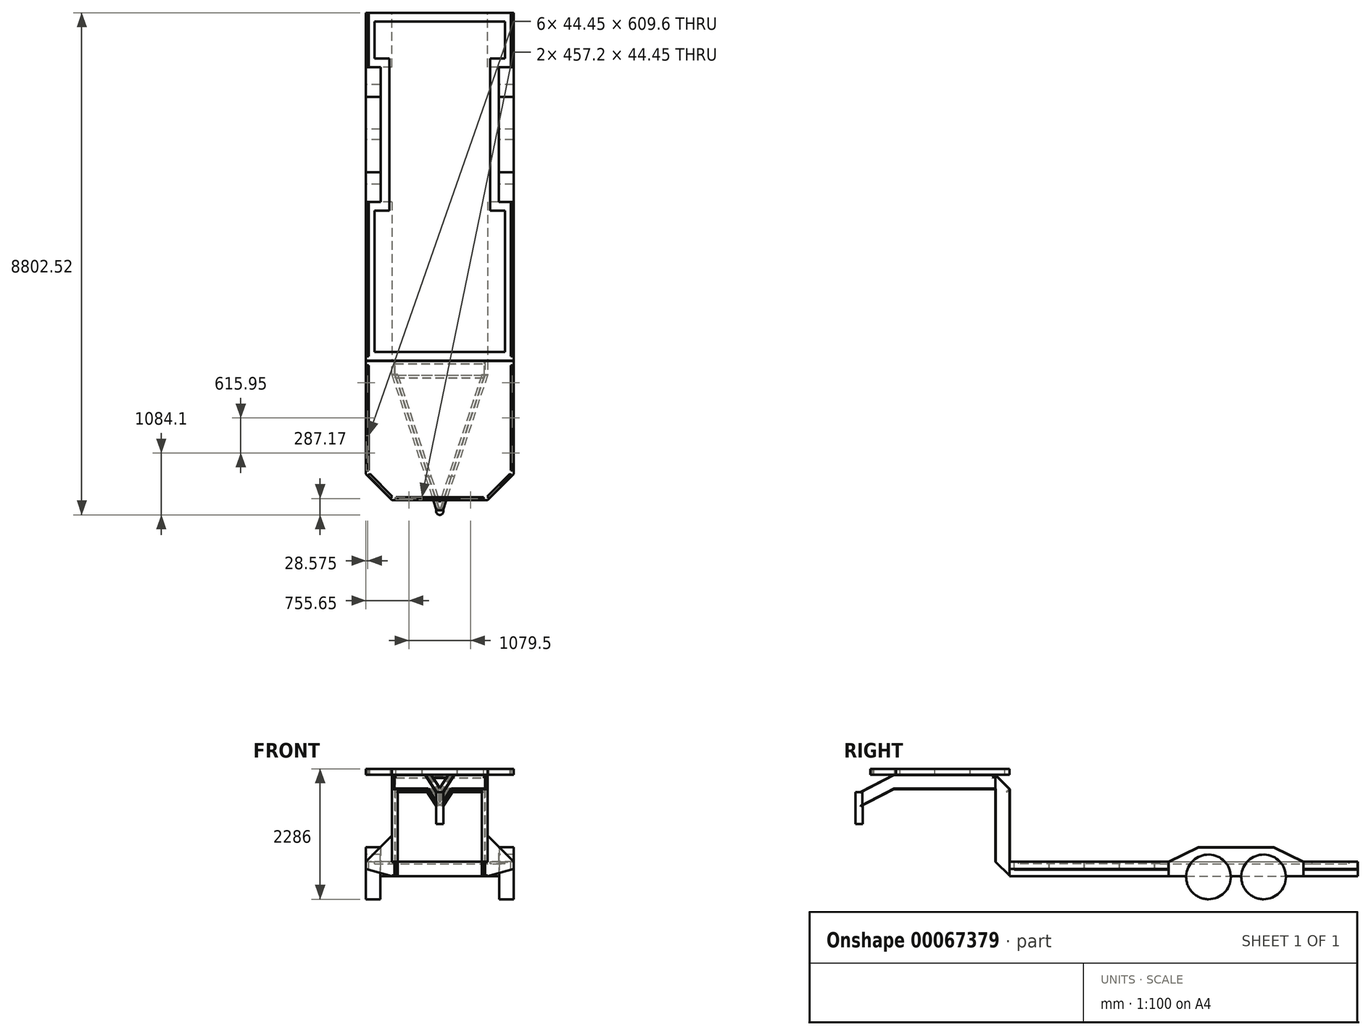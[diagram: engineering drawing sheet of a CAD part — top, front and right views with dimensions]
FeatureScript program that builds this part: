
annotation { "Feature Type Name" : "Feature", "Feature Type Description" : "" }
export const myFeature = defineFeature(function(context is Context, id is Id, definition is map)
    precondition{}
    {
        {
            var Q0;
            Q0=qCreatedBy(makeId("Front.planeOp"),FACE);
            var sketch = newSketch(context, id + "F0", { "sketchPlane" : qUnion([Q0])});
            skLineSegment(sketch, "E0.rect.bottom", {"start": v(1295.4, 660.4) * mm, "end": v(-1295.4, 660.4) * mm});
            skLineSegment(sketch, "E0.rect.top", {"start": v(1295.4, 406.4) * mm, "end": v(-1295.4, 406.4) * mm});
            skLineSegment(sketch, "E0.rect.left", {"start": v(1295.4, 660.4) * mm, "end": v(1295.4, 406.4) * mm});
            skLineSegment(sketch, "E0.rect.right", {"start": v(-1295.4, 660.4) * mm, "end": v(-1295.4, 406.4) * mm});
            skPoint(sketch, "E0.rect.middle", {"position": v(0, 533.4) * mm});
            skSolve(sketch);
        }
        {
            var Q0;
            Q0 = qSketchRegion(id + "F0", true);
            extrude(context, id + "F1", {"entities" : qUnion([Q0]), "depth" : 6096 * mm});
        }
        {
            var Q0;
            Q0=makeQuery(id+"F1.opExtrude","SWEPT_FACE",FACE,{"disambiguationData":[OSD([sQuery(id+"F0.wireOp",EDGE,"E0.rect.left")])]});
            var sketch = newSketch(context, id + "F2", { "sketchPlane" : qUnion([Q0])});
            skLineSegment(sketch, "E1", {"start": v(-3314.7, 660.4) * mm, "end": v(-2793.92, 914.4) * mm});
            skLineSegment(sketch, "E2", {"start": v(-2793.92, 914.4) * mm, "end": v(-1473.28, 914.4) * mm});
            skLineSegment(sketch, "E3", {"start": v(-1473.28, 914.4) * mm, "end": v(-952.5, 660.4) * mm});
            skLineSegment(sketch, "E4", {"start": v(-952.5, 660.4) * mm, "end": v(-3314.7, 660.4) * mm});
            skLineSegment(sketch, "E5", {"start": v(-2133.6, 660.4) * mm, "end": v(-2133.6, 406.4) * mm, "construction": true});
            skSolve(sketch);
        }
        {
            var Q0;
            Q0=makeQuery(id+"F2.imprint","IMPRINT",FACE,{"disambiguationData":[TD([[makeQuery(id+"F2.imprint","IMPRINT",EDGE,{"derivedFrom":sQuery(id+"F2.wireOp",EDGE,"E1")}),-1.0]])]});
            var Q1;
            Q1=makeQuery(id+"F1.opExtrude","SWEPT_FACE",FACE,{"disambiguationData":[OSD([sQuery(id+"F0.wireOp",EDGE,"E0.rect.right")])]});
            extrude(context, id + "F3", {"entities" : qUnion([Q0]), "operationType" : NewBodyOperationType.ADD, "endBound" : BoundingType.UP_TO_SURFACE, "oppositeDirection" : true, "endBoundEntityFace" : qUnion([Q1]), "depth" : 25.4 * mm});
        }
        {
            var Q0;
            Q0=makeQuery(id+"F3.boolean.opBoolean","MERGE",FACE,{"derivedFrom":[makeQuery(id+"F1.opExtrude","SWEPT_FACE",FACE,{"disambiguationData":[OSD([sQuery(id+"F0.wireOp",EDGE,"E0.rect.right")])]}),makeQuery(id+"F3.opExtrude","CAP_FACE",FACE,{"disambiguationData":[OSD([sQuery(id+"F2.wireOp",EDGE,"E1"),sQuery(id+"F2.wireOp",EDGE,"E2"),sQuery(id+"F2.wireOp",EDGE,"E3"),sQuery(id+"F2.wireOp",EDGE,"E4")])],"isStart":false})]});
            var sketch = newSketch(context, id + "F4", { "sketchPlane" : qUnion([Q0])});
            skCircle(sketch, "E6", {"center": v(1651, 391.16) * mm, "radius": 391.16 * mm});
            skCircle(sketch, "E7", {"center": v(2616.2, 391.16) * mm, "radius": 391.16 * mm});
            skLineSegment(sketch, "E8", {"start": v(2133.6, 914.4) * mm, "end": v(2133.6, 391.16) * mm, "construction": true});
            skLineSegment(sketch, "E9", {"start": v(1651, 391.16) * mm, "end": v(2616.2, 391.16) * mm, "construction": true});
            skSolve(sketch);
        }
        {
            var Q0;
            Q0 = qSketchRegion(id + "F4", true);
            var Q1;
            Q1=makeQuery(id+"F3.boolean.opBoolean","MERGE",FACE,{"derivedFrom":[makeQuery(id+"F1.opExtrude","SWEPT_FACE",FACE,{"disambiguationData":[OSD([sQuery(id+"F0.wireOp",EDGE,"E0.rect.left")])]}),makeQuery(id+"F3.opExtrude","CAP_FACE",FACE,{"disambiguationData":[OSD([sQuery(id+"F2.wireOp",EDGE,"E1"),sQuery(id+"F2.wireOp",EDGE,"E2"),sQuery(id+"F2.wireOp",EDGE,"E3"),sQuery(id+"F2.wireOp",EDGE,"E4")])],"isStart":true})]});
            extrude(context, id + "F5", {"entities" : qUnion([Q0]), "operationType" : NewBodyOperationType.ADD, "endBound" : BoundingType.UP_TO_SURFACE, "oppositeDirection" : true, "endBoundEntityFace" : qUnion([Q1]), "depth" : 25.4 * mm});
        }
        {
            var Q0;
            Q0=makeQuery(id+"F1.opExtrude","CAP_FACE",FACE,{"disambiguationData":[OSD([sQuery(id+"F0.wireOp",EDGE,"E0.rect.bottom"),sQuery(id+"F0.wireOp",EDGE,"E0.rect.top"),sQuery(id+"F0.wireOp",EDGE,"E0.rect.left"),sQuery(id+"F0.wireOp",EDGE,"E0.rect.right")])],"isStart":true});
            var sketch = newSketch(context, id + "F6", { "sketchPlane" : qUnion([Q0])});
            skLineSegment(sketch, "E10.bottom", {"start": v(-1035.05, 914.4) * mm, "end": v(1035.05, 914.4) * mm});
            skLineSegment(sketch, "E10.top", {"start": v(-1035.05, 660.4) * mm, "end": v(1035.05, 660.4) * mm});
            skLineSegment(sketch, "E10.left", {"start": v(-1035.05, 914.4) * mm, "end": v(-1035.05, 660.4) * mm});
            skLineSegment(sketch, "E10.right", {"start": v(1035.05, 914.4) * mm, "end": v(1035.05, 660.4) * mm});
            skLineSegment(sketch, "E11.bottom", {"start": v(-1041.4, 406.4) * mm, "end": v(1041.4, 406.4) * mm});
            skLineSegment(sketch, "E11.top", {"start": v(-1041.4, 0) * mm, "end": v(1041.4, 0) * mm});
            skLineSegment(sketch, "E11.left", {"start": v(-1041.4, 406.4) * mm, "end": v(-1041.4, 0) * mm});
            skLineSegment(sketch, "E11.right", {"start": v(1041.4, 406.4) * mm, "end": v(1041.4, 0) * mm});
            skLineSegment(sketch, "E12", {"start": v(-1295.4, 660.4) * mm, "end": v(-1035.05, 660.4) * mm, "construction": true});
            skLineSegment(sketch, "E13", {"start": v(-1295.4, 406.4) * mm, "end": v(-1041.4, 406.4) * mm, "construction": true});
            skLineSegment(sketch, "E14", {"start": v(1295.4, 406.4) * mm, "end": v(1041.4, 406.4) * mm, "construction": true});
            skLineSegment(sketch, "E15", {"start": v(1295.4, 660.4) * mm, "end": v(1035.05, 660.4) * mm, "construction": true});
            skSolve(sketch);
        }
        {
            var Q0;
            Q0=makeQuery(id+"F6.imprint","IMPRINT",FACE,{"disambiguationData":[TD([[makeQuery(id+"F6.imprint","IMPRINT",EDGE,{"derivedFrom":sQuery(id+"F6.wireOp",EDGE,"E10.bottom")}),-1.0]])]});
            var Q1;
            Q1=makeQuery(id+"F6.imprint","IMPRINT",FACE,{"disambiguationData":[TD([[makeQuery(id+"F6.imprint","IMPRINT",EDGE,{"derivedFrom":sQuery(id+"F6.wireOp",EDGE,"E11.bottom")}),-1.0]])]});
            extrude(context, id + "F7", {"entities" : qUnion([Q0, Q1]), "operationType" : NewBodyOperationType.REMOVE, "endBound" : BoundingType.THROUGH_ALL, "oppositeDirection" : true, "depth" : 25.4 * mm});
        }
        {
            var Q0;
            Q0=makeQuery(id+"F5.boolean.opBoolean","MERGE",FACE,{"derivedFrom":[makeQuery(id+"F3.boolean.opBoolean","MERGE",FACE,{"derivedFrom":[makeQuery(id+"F1.opExtrude","SWEPT_FACE",FACE,{"disambiguationData":[OSD([sQuery(id+"F0.wireOp",EDGE,"E0.rect.left")])]}),makeQuery(id+"F3.opExtrude","CAP_FACE",FACE,{"disambiguationData":[OSD([sQuery(id+"F2.wireOp",EDGE,"E1"),sQuery(id+"F2.wireOp",EDGE,"E2"),sQuery(id+"F2.wireOp",EDGE,"E3"),sQuery(id+"F2.wireOp",EDGE,"E4")])],"isStart":true})]}),makeQuery(id+"F5.opExtrude","CAP_FACE",FACE,{"disambiguationData":[OSD([sQuery(id+"F4.wireOp",EDGE,"E6")])],"isStart":false}),makeQuery(id+"F5.opExtrude","CAP_FACE",FACE,{"disambiguationData":[OSD([sQuery(id+"F4.wireOp",EDGE,"E7")])],"isStart":false})]});
            var sketch = newSketch(context, id + "F8", { "sketchPlane" : qUnion([Q0])});
            skLineSegment(sketch, "E16", {"start": v(-3314.7, 653.33) * mm, "end": v(-2792.46, 908.05) * mm});
            skLineSegment(sketch, "E17", {"start": v(-2792.46, 908.05) * mm, "end": v(-1474.74, 908.05) * mm});
            skLineSegment(sketch, "E18", {"start": v(-1474.74, 908.05) * mm, "end": v(-952.5, 653.33) * mm});
            skLineSegment(sketch, "E19", {"start": v(-952.5, 653.33) * mm, "end": v(-952.5, 406.4) * mm});
            skLineSegment(sketch, "E20", {"start": v(-952.5, 406.4) * mm, "end": v(-1260.14, 406.4) * mm});
            skLineSegment(sketch, "E21", {"start": v(-3314.7, 653.33) * mm, "end": v(-3314.7, 406.4) * mm});
            skLineSegment(sketch, "E22", {"start": v(-3314.7, 406.4) * mm, "end": v(-3007.06, 406.4) * mm});
            skLineSegment(sketch, "E23", {"start": v(-2225.34, 406.4) * mm, "end": v(-2041.86, 406.4) * mm});
            skArc(sketch, "E24", {"start": v(-2225.34, 406.4) * mm, "mid": v(-2616.2, 782.32) * mm, "end": v(-3007.06, 406.4) * mm});
            skArc(sketch, "E25", {"start": v(-1260.14, 406.4) * mm, "mid": v(-1651, 782.32) * mm, "end": v(-2041.86, 406.4) * mm});
            skSolve(sketch);
        }
        {
            var Q0;
            Q0 = qSketchRegion(id + "F8", true);
            extrude(context, id + "F9", {"entities" : qUnion([Q0]), "operationType" : NewBodyOperationType.REMOVE, "oppositeDirection" : true, "depth" : 254 * mm});
        }
        {
            var Q0;
            Q0=makeQuery(id+"F5.boolean.opBoolean","MERGE",FACE,{"derivedFrom":[makeQuery(id+"F3.boolean.opBoolean","MERGE",FACE,{"derivedFrom":[makeQuery(id+"F1.opExtrude","SWEPT_FACE",FACE,{"disambiguationData":[OSD([sQuery(id+"F0.wireOp",EDGE,"E0.rect.right")])]}),makeQuery(id+"F3.opExtrude","CAP_FACE",FACE,{"disambiguationData":[OSD([sQuery(id+"F2.wireOp",EDGE,"E1"),sQuery(id+"F2.wireOp",EDGE,"E2"),sQuery(id+"F2.wireOp",EDGE,"E3"),sQuery(id+"F2.wireOp",EDGE,"E4")])],"isStart":false})]}),makeQuery(id+"F5.opExtrude","CAP_FACE",FACE,{"disambiguationData":[OSD([sQuery(id+"F4.wireOp",EDGE,"E6")])],"isStart":true}),makeQuery(id+"F5.opExtrude","CAP_FACE",FACE,{"disambiguationData":[OSD([sQuery(id+"F4.wireOp",EDGE,"E7")])],"isStart":true})]});
            var sketch = newSketch(context, id + "F10", { "sketchPlane" : qUnion([Q0])});
            skLineSegment(sketch, "E26", {"start": v(952.5, 653.33) * mm, "end": v(1474.74, 908.05) * mm});
            skLineSegment(sketch, "E27", {"start": v(1474.74, 908.05) * mm, "end": v(2792.46, 908.05) * mm});
            skLineSegment(sketch, "E28", {"start": v(2792.46, 908.05) * mm, "end": v(3314.7, 653.33) * mm});
            skLineSegment(sketch, "E29", {"start": v(3314.7, 653.33) * mm, "end": v(3314.7, 406.4) * mm});
            skLineSegment(sketch, "E30", {"start": v(3314.7, 406.4) * mm, "end": v(3007.06, 406.4) * mm});
            skArc(sketch, "E31", {"start": v(3007.06, 406.4) * mm, "mid": v(2616.2, 782.32) * mm, "end": v(2225.34, 406.4) * mm});
            skArc(sketch, "E32", {"start": v(2041.86, 406.4) * mm, "mid": v(1651, 782.32) * mm, "end": v(1260.14, 406.4) * mm});
            skLineSegment(sketch, "E33", {"start": v(2041.86, 406.4) * mm, "end": v(2225.34, 406.4) * mm});
            skLineSegment(sketch, "E34", {"start": v(952.5, 653.33) * mm, "end": v(952.5, 406.4) * mm});
            skLineSegment(sketch, "E35", {"start": v(952.5, 406.4) * mm, "end": v(1260.14, 406.4) * mm});
            skSolve(sketch);
        }
        {
            var Q0;
            Q0=makeQuery(id+"F10.imprint","IMPRINT",FACE,{"disambiguationData":[TD([[makeQuery(id+"F10.imprint","IMPRINT",EDGE,{"derivedFrom":sQuery(id+"F10.wireOp",EDGE,"E26")}),-1.0]])]});
            extrude(context, id + "F11", {"entities" : qUnion([Q0]), "operationType" : NewBodyOperationType.REMOVE, "oppositeDirection" : true, "depth" : 254 * mm});
        }
        {
            var Q0;
            {var subQ0=sQuery(id+"F2.wireOp",EDGE,"E4");var subQ1=sQuery(id+"F2.wireOp",EDGE,"E3");var subQ2=sQuery(id+"F2.wireOp",EDGE,"E2");var subQ3=sQuery(id+"F2.wireOp",EDGE,"E1");var subQ4=makeQuery(id+"F3.opExtrude","CAP_FACE",FACE,{"disambiguationData":[OSD([subQ3,subQ2,subQ1,subQ0])],"isStart":false});var subQ5=sQuery(id+"F0.wireOp",EDGE,"E0.rect.right");var subQ6=makeQuery(id+"F1.opExtrude","SWEPT_FACE",FACE,{"disambiguationData":[OSD([subQ5])]});var subQ7=makeQuery(id+"F3.opExtrude","CAP_FACE",FACE,{"disambiguationData":[OSD([subQ3,subQ2,subQ1,subQ0])],"isStart":true});var subQ8=sQuery(id+"F0.wireOp",EDGE,"E0.rect.left");var subQ9=makeQuery(id+"F1.opExtrude","SWEPT_FACE",FACE,{"disambiguationData":[OSD([subQ8])]});var subQ10=sQuery(id+"F4.wireOp",EDGE,"E6");var subQ11=makeQuery(id+"F5.opExtrude","SWEPT_FACE",FACE,{"disambiguationData":[OSD([subQ10])]});var subQ12=makeQuery(id+"F5.opExtrude","CAP_FACE",FACE,{"disambiguationData":[OSD([subQ10])],"isStart":true});var subQ13=makeQuery(id+"F5.opExtrude","CAP_FACE",FACE,{"disambiguationData":[OSD([subQ10])],"isStart":false});var subQ14=sQuery(id+"F4.wireOp",EDGE,"E7");var subQ15=makeQuery(id+"F5.opExtrude","SWEPT_FACE",FACE,{"disambiguationData":[OSD([subQ14])]});var subQ16=makeQuery(id+"F5.opExtrude","CAP_FACE",FACE,{"disambiguationData":[OSD([subQ14])],"isStart":true});var subQ17=makeQuery(id+"F5.opExtrude","CAP_FACE",FACE,{"disambiguationData":[OSD([subQ14])],"isStart":false});var subQ18=sQuery(id+"F0.wireOp",EDGE,"E0.rect.top");var subQ19=makeQuery(id+"F1.opExtrude","SWEPT_FACE",FACE,{"disambiguationData":[OSD([subQ18])]});var subQ20=sQuery(id+"F0.wireOp",EDGE,"E0.rect.bottom");Q0=makeQuery(id+"F7.boolean.opBoolean","MERGE",FACE,{"derivedFrom":[makeQuery(id+"F5.boolean.opBoolean","SPLIT",FACE,{"disambiguationData":[TD([makeQuery(id+"F1.opExtrude","CAP_FACE",FACE,{"disambiguationData":[OSD([subQ20,subQ18,subQ8,subQ5])],"isStart":true}),subQ9,subQ6,subQ7,subQ4,subQ11,subQ12,subQ13,subQ16,subQ17])],"derivedFrom":subQ19}),makeQuery(id+"F5.boolean.opBoolean","SPLIT",FACE,{"disambiguationData":[TD([makeQuery(id+"F1.opExtrude","CAP_FACE",FACE,{"disambiguationData":[OSD([subQ20,subQ18,subQ8,subQ5])],"isStart":false}),subQ9,subQ6,subQ7,subQ4,subQ12,subQ13,subQ15,subQ16,subQ17])],"derivedFrom":subQ19}),makeQuery(id+"F5.boolean.opBoolean","SPLIT",FACE,{"disambiguationData":[TD([subQ9,subQ6,subQ7,subQ4,subQ11,subQ12,subQ13,subQ15,subQ16,subQ17])],"derivedFrom":subQ19})],"fromTools":[makeQuery(id+"F7.opExtrude","SWEPT_FACE",FACE,{"disambiguationData":[OSD([sQuery(id+"F6.wireOp",EDGE,"E11.bottom")])]})]});}
            var sketch = newSketch(context, id + "F12", { "sketchPlane" : qUnion([Q0])});
            skLineSegment(sketch, "E36", {"start": v(838.2, 6096) * mm, "end": v(838.2, 6105.53) * mm});
            skLineSegment(sketch, "E37", {"start": v(838.2, 6105.53) * mm, "end": v(792.16, 6105.53) * mm});
            skLineSegment(sketch, "E38", {"start": v(792.16, 6105.53) * mm, "end": v(792.16, 6340.48) * mm});
            skLineSegment(sketch, "E39", {"start": v(792.16, 6340.48) * mm, "end": v(838.2, 6340.48) * mm});
            skLineSegment(sketch, "E40", {"start": v(838.2, 6340.48) * mm, "end": v(838.2, 6350) * mm});
            skLineSegment(sketch, "E41", {"start": v(838.2, 6350) * mm, "end": v(736.6, 6350) * mm});
            skLineSegment(sketch, "E42", {"start": v(736.6, 6350) * mm, "end": v(736.6, 6340.48) * mm});
            skLineSegment(sketch, "E43", {"start": v(736.6, 6340.48) * mm, "end": v(782.64, 6340.48) * mm});
            skLineSegment(sketch, "E44", {"start": v(782.64, 6340.48) * mm, "end": v(782.64, 6105.53) * mm});
            skLineSegment(sketch, "E45", {"start": v(782.64, 6105.53) * mm, "end": v(736.6, 6105.53) * mm});
            skLineSegment(sketch, "E46", {"start": v(736.6, 6105.53) * mm, "end": v(736.6, 6096) * mm});
            skLineSegment(sketch, "E47", {"start": v(736.6, 6096) * mm, "end": v(838.2, 6096) * mm});
            skLineSegment(sketch, "E48", {"start": v(792.16, 6340.48) * mm, "end": v(782.64, 6340.48) * mm, "construction": true});
            skLineSegment(sketch, "E49", {"start": v(0, 6096) * mm, "end": v(0, 0) * mm, "construction": true});
            skLineSegment(sketch, "E50.MirrorCS", {"start": v(-792.16, 6340.48) * mm, "end": v(-782.64, 6340.48) * mm, "construction": true});
            skLineSegment(sketch, "E51.MirrorCS", {"start": v(-736.6, 6340.48) * mm, "end": v(-782.64, 6340.48) * mm});
            skLineSegment(sketch, "E52.MirrorCS", {"start": v(-736.6, 6350) * mm, "end": v(-736.6, 6340.48) * mm});
            skLineSegment(sketch, "E53.MirrorCS", {"start": v(-838.2, 6096) * mm, "end": v(-838.2, 6105.53) * mm});
            skLineSegment(sketch, "E54.MirrorCS", {"start": v(-792.16, 6340.48) * mm, "end": v(-838.2, 6340.48) * mm});
            skLineSegment(sketch, "E55.MirrorCS", {"start": v(-838.2, 6340.48) * mm, "end": v(-838.2, 6350) * mm});
            skLineSegment(sketch, "E56.MirrorCS", {"start": v(-838.2, 6350) * mm, "end": v(-736.6, 6350) * mm});
            skLineSegment(sketch, "E57.MirrorCS", {"start": v(-736.6, 6096) * mm, "end": v(-838.2, 6096) * mm});
            skLineSegment(sketch, "E58.MirrorCS", {"start": v(-736.6, 6105.53) * mm, "end": v(-736.6, 6096) * mm});
            skLineSegment(sketch, "E59.MirrorCS", {"start": v(-838.2, 6105.53) * mm, "end": v(-792.16, 6105.53) * mm});
            skLineSegment(sketch, "E60.MirrorCS", {"start": v(-782.64, 6105.53) * mm, "end": v(-736.6, 6105.53) * mm});
            skLineSegment(sketch, "E61.MirrorCS", {"start": v(-792.16, 6105.53) * mm, "end": v(-792.16, 6340.48) * mm});
            skLineSegment(sketch, "E62.MirrorCS", {"start": v(-782.64, 6340.48) * mm, "end": v(-782.64, 6105.53) * mm});
            skSolve(sketch);
        }
        {
            var Q0;
            Q0=makeQuery(id+"F12.imprint","IMPRINT",FACE,{"disambiguationData":[TD([[makeQuery(id+"F12.imprint","IMPRINT",EDGE,{"derivedFrom":sQuery(id+"F12.wireOp",EDGE,"E51.MirrorCS")}),-1.0]])]});
            var Q1;
            Q1=makeQuery(id+"F12.imprint","IMPRINT",FACE,{"disambiguationData":[TD([[makeQuery(id+"F12.imprint","IMPRINT",EDGE,{"derivedFrom":sQuery(id+"F12.wireOp",EDGE,"E36")}),1.0]])]});
            extrude(context, id + "F13", {"entities" : qUnion([Q0, Q1]), "operationType" : NewBodyOperationType.ADD, "oppositeDirection" : true, "depth" : 1524 * mm});
        }
        {
            var Q0;
            Q0=makeQuery(id+"F13.opExtrude","CAP_FACE",FACE,{"disambiguationData":[OSD([sQuery(id+"F12.wireOp",EDGE,"E36"),sQuery(id+"F12.wireOp",EDGE,"E37"),sQuery(id+"F12.wireOp",EDGE,"E38"),sQuery(id+"F12.wireOp",EDGE,"E39"),sQuery(id+"F12.wireOp",EDGE,"E40"),sQuery(id+"F12.wireOp",EDGE,"E41"),sQuery(id+"F12.wireOp",EDGE,"E42"),sQuery(id+"F12.wireOp",EDGE,"E43"),sQuery(id+"F12.wireOp",EDGE,"E44"),sQuery(id+"F12.wireOp",EDGE,"E45"),sQuery(id+"F12.wireOp",EDGE,"E46"),sQuery(id+"F12.wireOp",EDGE,"E47")])],"isStart":false});
            var sketch = newSketch(context, id + "F14", { "sketchPlane" : qUnion([Q0])});
            skLineSegment(sketch, "E63", {"start": v(-787.4, -6350) * mm, "end": v(-201.04, -8128) * mm});
            skLineSegment(sketch, "E64", {"start": v(-201.04, -8128) * mm, "end": v(0, -8737.6) * mm});
            skLineSegment(sketch, "E65", {"start": v(0, -8737.6) * mm, "end": v(201.04, -8128) * mm});
            skLineSegment(sketch, "E66", {"start": v(201.04, -8128) * mm, "end": v(787.4, -6350) * mm});
            skSolve(sketch);
        }
        {
            var Q0;
            {var subQ1=sQuery(id+"F0.wireOp",EDGE,"E0.rect.left");var subQ3=sQuery(id+"F0.wireOp",EDGE,"E0.rect.bottom");var subQ4=sQuery(id+"F2.wireOp",EDGE,"E3");var subQ5=sQuery(id+"F2.wireOp",EDGE,"E2");var subQ6=sQuery(id+"F2.wireOp",EDGE,"E1");Q0=makeQuery(id+"F9.boolean.opBoolean","SPLIT",FACE,{"disambiguationData":[TD([makeQuery(id+"F1.opExtrude","SWEPT_FACE",FACE,{"disambiguationData":[OSD([subQ3])]})])],"derivedFrom":makeQuery(id+"F5.boolean.opBoolean","MERGE",FACE,{"derivedFrom":[makeQuery(id+"F3.boolean.opBoolean","MERGE",FACE,{"derivedFrom":[makeQuery(id+"F1.opExtrude","SWEPT_FACE",FACE,{"disambiguationData":[OSD([subQ1])]}),makeQuery(id+"F3.opExtrude","CAP_FACE",FACE,{"disambiguationData":[OSD([subQ6,subQ5,subQ4,sQuery(id+"F2.wireOp",EDGE,"E4")])],"isStart":true})]}),makeQuery(id+"F5.opExtrude","CAP_FACE",FACE,{"disambiguationData":[OSD([sQuery(id+"F4.wireOp",EDGE,"E6")])],"isStart":false}),makeQuery(id+"F5.opExtrude","CAP_FACE",FACE,{"disambiguationData":[OSD([sQuery(id+"F4.wireOp",EDGE,"E7")])],"isStart":false})]})});}
            var sketch = newSketch(context, id + "F15", { "sketchPlane" : qUnion([Q0])});
            skLineSegment(sketch, "E67", {"start": v(-6096, 406.4) * mm, "end": v(-6350, 660.4) * mm});
            skLineSegment(sketch, "E68", {"start": v(-6350, 660.4) * mm, "end": v(-6350, 406.4) * mm});
            skLineSegment(sketch, "E69", {"start": v(-6350, 406.4) * mm, "end": v(-6096, 406.4) * mm});
            skSolve(sketch);
        }
        {
            var Q0;
            Q0=makeQuery(id+"F15.imprint","IMPRINT",FACE,{"disambiguationData":[TD([[makeQuery(id+"F15.imprint","IMPRINT",EDGE,{"derivedFrom":sQuery(id+"F15.wireOp",EDGE,"E67")}),1.0]])]});
            extrude(context, id + "F16", {"entities" : qUnion([Q0]), "operationType" : NewBodyOperationType.REMOVE, "endBound" : BoundingType.THROUGH_ALL, "oppositeDirection" : true, "depth" : 25.4 * mm});
        }
        {
            var Q0;
            Q0=makeQuery(id+"F13.opExtrude","SWEPT_FACE",FACE,{"disambiguationData":[OSD([sQuery(id+"F12.wireOp",EDGE,"E41")])]});
            var sketch = newSketch(context, id + "F17", { "sketchPlane" : qUnion([Q0])});
            skLineSegment(sketch, "E70", {"start": v(736.6, 1930.4) * mm, "end": v(838.2, 1930.4) * mm});
            skLineSegment(sketch, "E71", {"start": v(838.2, 1930.4) * mm, "end": v(838.2, 1939.93) * mm});
            skLineSegment(sketch, "E72", {"start": v(838.2, 1939.93) * mm, "end": v(792.16, 1939.93) * mm});
            skLineSegment(sketch, "E73", {"start": v(792.16, 1939.93) * mm, "end": v(792.16, 2174.88) * mm});
            skLineSegment(sketch, "E74", {"start": v(792.16, 2174.88) * mm, "end": v(838.2, 2174.88) * mm});
            skLineSegment(sketch, "E75", {"start": v(838.2, 2174.88) * mm, "end": v(838.2, 2184.4) * mm});
            skLineSegment(sketch, "E76", {"start": v(838.2, 2184.4) * mm, "end": v(736.6, 2184.4) * mm});
            skLineSegment(sketch, "E77", {"start": v(736.6, 2184.4) * mm, "end": v(736.6, 2174.88) * mm});
            skLineSegment(sketch, "E78", {"start": v(736.6, 2174.88) * mm, "end": v(782.64, 2174.88) * mm});
            skLineSegment(sketch, "E79", {"start": v(782.64, 2174.88) * mm, "end": v(782.64, 1939.93) * mm});
            skLineSegment(sketch, "E80", {"start": v(782.64, 1939.93) * mm, "end": v(736.6, 1939.93) * mm});
            skLineSegment(sketch, "E81", {"start": v(736.6, 1939.93) * mm, "end": v(736.6, 1930.4) * mm});
            skLineSegment(sketch, "E82", {"start": v(782.64, 1939.93) * mm, "end": v(792.16, 1939.93) * mm, "construction": true});
            skLineSegment(sketch, "E83", {"start": v(0, 406.4) * mm, "end": v(0, 660.4) * mm, "construction": true});
            skLineSegment(sketch, "E84.MirrorCS", {"start": v(-782.64, 1939.93) * mm, "end": v(-792.16, 1939.93) * mm, "construction": true});
            skLineSegment(sketch, "E85.MirrorCS", {"start": v(-782.64, 1939.93) * mm, "end": v(-736.6, 1939.93) * mm});
            skLineSegment(sketch, "E86.MirrorCS", {"start": v(-736.6, 1939.93) * mm, "end": v(-736.6, 1930.4) * mm});
            skLineSegment(sketch, "E87.MirrorCS", {"start": v(-736.6, 1930.4) * mm, "end": v(-838.2, 1930.4) * mm});
            skLineSegment(sketch, "E88.MirrorCS", {"start": v(-838.2, 1930.4) * mm, "end": v(-838.2, 1939.93) * mm});
            skLineSegment(sketch, "E89.MirrorCS", {"start": v(-838.2, 1939.93) * mm, "end": v(-792.16, 1939.93) * mm});
            skLineSegment(sketch, "E90.MirrorCS", {"start": v(-792.16, 2174.88) * mm, "end": v(-838.2, 2174.88) * mm});
            skLineSegment(sketch, "E91.MirrorCS", {"start": v(-838.2, 2184.4) * mm, "end": v(-736.6, 2184.4) * mm});
            skLineSegment(sketch, "E92.MirrorCS", {"start": v(-736.6, 2174.88) * mm, "end": v(-782.64, 2174.88) * mm});
            skLineSegment(sketch, "E93.MirrorCS", {"start": v(-736.6, 2184.4) * mm, "end": v(-736.6, 2174.88) * mm});
            skLineSegment(sketch, "E94.MirrorCS", {"start": v(-838.2, 2174.88) * mm, "end": v(-838.2, 2184.4) * mm});
            skLineSegment(sketch, "E95.MirrorCS", {"start": v(-792.16, 1939.93) * mm, "end": v(-792.16, 2174.88) * mm});
            skLineSegment(sketch, "E96.MirrorCS", {"start": v(-782.64, 2174.88) * mm, "end": v(-782.64, 1939.93) * mm});
            skSolve(sketch);
        }
        {
            var Q1;
            Q1=makeQuery(id+"F14.imprint","IMPRINT",FACE,{"disambiguationData":[TD([[makeQuery(id+"F14.imprint","IMPRINT",EDGE,{"derivedFrom":makeQuery(id+"F13.opExtrude","CAP_EDGE",EDGE,{"disambiguationData":[OSD([sQuery(id+"F12.wireOp",EDGE,"E36")])],"isStart":false})}),-1.0]])]});
            var Q2;
            Q2=makeQuery(id+"F17.imprint","IMPRINT",FACE,{"disambiguationData":[TD([[makeQuery(id+"F17.imprint","IMPRINT",EDGE,{"derivedFrom":sQuery(id+"F17.wireOp",EDGE,"E70")}),-1.0]])]});
            var Q3;
            Q3=sQuery(id+"F17.wireOp",VERTEX,"E80.end");
            var Q4;
            Q4=makeQuery(id+"F13.opExtrude","CAP_VERTEX",VERTEX,{"disambiguationData":[OSD([sQuery(id+"F12.wireOp",EDGE,"E42"),sQuery(id+"F12.wireOp",EDGE,"E43")])],"isStart":false});
            loft(context, id + "F18", {"operationType" : NewBodyOperationType.ADD, "sheetProfilesArray" : [{ "sheetProfileEntities" : qUnion([Q1]) }, { "sheetProfileEntities" : qUnion([Q2]) }], "matchConnections" : true, "connections" : [{ "connectionEntities" : qUnion([Q3, Q4]), "connectionEdgeQueries" : qUnion([]), "connectionEdgeParameters" : [] }]});
        }
        {
            var Q1;
            Q1=makeQuery(id+"F17.imprint","IMPRINT",FACE,{"disambiguationData":[TD([[makeQuery(id+"F17.imprint","IMPRINT",EDGE,{"derivedFrom":sQuery(id+"F17.wireOp",EDGE,"E85.MirrorCS")}),-1.0]])]});
            var Q2;
            Q2=makeQuery(id+"F13.opExtrude","CAP_FACE",FACE,{"disambiguationData":[OSD([sQuery(id+"F12.wireOp",EDGE,"E51.MirrorCS"),sQuery(id+"F12.wireOp",EDGE,"E52.MirrorCS"),sQuery(id+"F12.wireOp",EDGE,"E53.MirrorCS"),sQuery(id+"F12.wireOp",EDGE,"E54.MirrorCS"),sQuery(id+"F12.wireOp",EDGE,"E55.MirrorCS"),sQuery(id+"F12.wireOp",EDGE,"E56.MirrorCS"),sQuery(id+"F12.wireOp",EDGE,"E57.MirrorCS"),sQuery(id+"F12.wireOp",EDGE,"E58.MirrorCS"),sQuery(id+"F12.wireOp",EDGE,"E59.MirrorCS"),sQuery(id+"F12.wireOp",EDGE,"E60.MirrorCS"),sQuery(id+"F12.wireOp",EDGE,"E61.MirrorCS"),sQuery(id+"F12.wireOp",EDGE,"E62.MirrorCS")])],"isStart":false});
            loft(context, id + "F19", {"operationType" : NewBodyOperationType.ADD, "sheetProfilesArray" : [{ "sheetProfileEntities" : qUnion([Q1]) }, { "sheetProfileEntities" : qUnion([Q2]) }]});
        }
        {
            var Q0;
            Q0 = qSketchRegion(id + "F14", true);
            var Q1;
            Q1=makeQuery(id+"F17.imprint","IMPRINT",FACE,{"disambiguationData":[TD([[makeQuery(id+"F17.imprint","IMPRINT",EDGE,{"derivedFrom":sQuery(id+"F17.wireOp",EDGE,"E70")}),-1.0]])]});
            var Q2;
            Q2=sQuery(id+"F14.wireOp",EDGE,"E66");
            sweep(context, id + "F20", {"operationType" : NewBodyOperationType.ADD, "profiles" : qUnion([Q0, Q1]), "path" : qUnion([Q2]), "keepProfileOrientation" : true});
        }
        {
            var Q0;
            Q0=makeQuery(id+"F17.imprint","IMPRINT",FACE,{"disambiguationData":[TD([[makeQuery(id+"F17.imprint","IMPRINT",EDGE,{"derivedFrom":sQuery(id+"F17.wireOp",EDGE,"E85.MirrorCS")}),-1.0]])]});
            var Q1;
            Q1=sQuery(id+"F14.wireOp",EDGE,"E63");
            sweep(context, id + "F21", {"operationType" : NewBodyOperationType.ADD, "profiles" : qUnion([Q0]), "path" : qUnion([Q1]), "keepProfileOrientation" : true});
        }
        {
            var Q0;
            Q0=makeQuery(id+"F20.opSweep","SWEPT_FACE",FACE,{"disambiguationData":[OSD([sQuery(id+"F14.wireOp",EDGE,"E66"),sQuery(id+"F17.wireOp",EDGE,"E73")])]});
            var sketch = newSketch(context, id + "F22", { "sketchPlane" : qUnion([Q0])});
            skLineSegment(sketch, "E97", {"start": v(-7654.61, 1939.92) * mm, "end": v(-8298, 1625.6) * mm});
            skSolve(sketch);
        }
        {
            var Q0;
            Q0=makeQuery(id+"F20.opSweep","CAP_FACE",FACE,{"disambiguationData":[OSD([sQuery(id+"F14.wireOp",VERTEX,"E66.start"),sQuery(id+"F17.wireOp",EDGE,"E70"),sQuery(id+"F17.wireOp",EDGE,"E71"),sQuery(id+"F17.wireOp",EDGE,"E72"),sQuery(id+"F17.wireOp",EDGE,"E73"),sQuery(id+"F17.wireOp",EDGE,"E74"),sQuery(id+"F17.wireOp",EDGE,"E75"),sQuery(id+"F17.wireOp",EDGE,"E76"),sQuery(id+"F17.wireOp",EDGE,"E77"),sQuery(id+"F17.wireOp",EDGE,"E78"),sQuery(id+"F17.wireOp",EDGE,"E79"),sQuery(id+"F17.wireOp",EDGE,"E80"),sQuery(id+"F17.wireOp",EDGE,"E81")])],"isStart":false});
            var Q1;
            Q1=sQuery(id+"F22.wireOp",EDGE,"E97");
            sweep(context, id + "F23", {"operationType" : NewBodyOperationType.ADD, "profiles" : qUnion([Q0]), "path" : qUnion([Q1])});
        }
        {
            var Q0;
            Q0=makeQuery(id+"F21.opSweep","SWEPT_FACE",FACE,{"disambiguationData":[OSD([sQuery(id+"F14.wireOp",EDGE,"E63"),sQuery(id+"F17.wireOp",EDGE,"E95.MirrorCS")])]});
            var sketch = newSketch(context, id + "F24", { "sketchPlane" : qUnion([Q0])});
            skLineSegment(sketch, "E98", {"start": v(7654.61, 1939.93) * mm, "end": v(8298, 1625.6) * mm});
            skSolve(sketch);
        }
        {
            var Q0;
            Q0=makeQuery(id+"F21.opSweep","CAP_FACE",FACE,{"disambiguationData":[OSD([sQuery(id+"F14.wireOp",VERTEX,"E63.end"),sQuery(id+"F17.wireOp",EDGE,"E85.MirrorCS"),sQuery(id+"F17.wireOp",EDGE,"E86.MirrorCS"),sQuery(id+"F17.wireOp",EDGE,"E87.MirrorCS"),sQuery(id+"F17.wireOp",EDGE,"E88.MirrorCS"),sQuery(id+"F17.wireOp",EDGE,"E89.MirrorCS"),sQuery(id+"F17.wireOp",EDGE,"E90.MirrorCS"),sQuery(id+"F17.wireOp",EDGE,"E91.MirrorCS"),sQuery(id+"F17.wireOp",EDGE,"E92.MirrorCS"),sQuery(id+"F17.wireOp",EDGE,"E93.MirrorCS"),sQuery(id+"F17.wireOp",EDGE,"E94.MirrorCS"),sQuery(id+"F17.wireOp",EDGE,"E95.MirrorCS"),sQuery(id+"F17.wireOp",EDGE,"E96.MirrorCS")])],"isStart":false});
            var Q1;
            Q1=sQuery(id+"F24.wireOp",EDGE,"E98");
            sweep(context, id + "F25", {"operationType" : NewBodyOperationType.ADD, "profiles" : qUnion([Q0]), "path" : qUnion([Q1])});
        }
        {
            var Q0;
            {var subQ0=sQuery(id+"F12.wireOp",EDGE,"E44");Q0=makeQuery(id+"F18.boolean.opBoolean","MERGE",FACE,{"derivedFrom":[makeQuery(id+"F13.opExtrude","SWEPT_FACE",FACE,{"disambiguationData":[OSD([subQ0])]}),makeQuery(id+"F18.opLoft","SWEPT_FACE",FACE,{"disambiguationData":[OSD([sQuery(id+"F12.wireOp",EDGE,"E43"),subQ0,sQuery(id+"F12.wireOp",EDGE,"E45"),sQuery(id+"F17.wireOp",EDGE,"E78"),sQuery(id+"F17.wireOp",EDGE,"E79"),sQuery(id+"F17.wireOp",EDGE,"E80")])]})]});}
            var sketch = newSketch(context, id + "F26", { "sketchPlane" : qUnion([Q0])});
            skLineSegment(sketch, "E99", {"start": v(6149.88, 1876.52) * mm, "end": v(6096, 1930.4) * mm});
            skLineSegment(sketch, "E100", {"start": v(6096, 1930.4) * mm, "end": v(6350, 2184.4) * mm});
            skLineSegment(sketch, "E101", {"start": v(6350, 2184.4) * mm, "end": v(6403.88, 2130.52) * mm});
            skLineSegment(sketch, "E102", {"start": v(6403.88, 2130.52) * mm, "end": v(6397.15, 2123.78) * mm});
            skLineSegment(sketch, "E103", {"start": v(6397.15, 2123.78) * mm, "end": v(6354.76, 2166.17) * mm});
            skLineSegment(sketch, "E104", {"start": v(6354.76, 2166.17) * mm, "end": v(6114.23, 1925.64) * mm});
            skLineSegment(sketch, "E105", {"start": v(6114.23, 1925.64) * mm, "end": v(6156.62, 1883.25) * mm});
            skLineSegment(sketch, "E106", {"start": v(6156.62, 1883.25) * mm, "end": v(6149.88, 1876.52) * mm});
            skLineSegment(sketch, "E107", {"start": v(6234.5, 2045.9) * mm, "end": v(6227.76, 2052.64) * mm, "construction": true});
            skSolve(sketch);
        }
        {
            var Q0;
            Q0 = qSketchRegion(id + "F26", true);
            var Q1;
            {var subQ0=sQuery(id+"F12.wireOp",EDGE,"E62.MirrorCS");Q1=makeQuery(id+"F19.boolean.opBoolean","MERGE",FACE,{"derivedFrom":[makeQuery(id+"F13.opExtrude","SWEPT_FACE",FACE,{"disambiguationData":[OSD([subQ0])]}),makeQuery(id+"F19.opLoft","SWEPT_FACE",FACE,{"disambiguationData":[OSD([sQuery(id+"F12.wireOp",EDGE,"E51.MirrorCS"),sQuery(id+"F12.wireOp",EDGE,"E60.MirrorCS"),subQ0,sQuery(id+"F17.wireOp",EDGE,"E85.MirrorCS"),sQuery(id+"F17.wireOp",EDGE,"E92.MirrorCS"),sQuery(id+"F17.wireOp",EDGE,"E96.MirrorCS")])]})]});}
            extrude(context, id + "F27", {"entities" : qUnion([Q0]), "operationType" : NewBodyOperationType.ADD, "endBound" : BoundingType.UP_TO_SURFACE, "endBoundEntityFace" : qUnion([Q1]), "depth" : 25.4 * mm});
        }
        {
            var Q0;
            {var subQ6=sQuery(id+"F0.wireOp",EDGE,"E0.rect.left");var subQ7=sQuery(id+"F0.wireOp",EDGE,"E0.rect.bottom");var subQ8=sQuery(id+"F0.wireOp",EDGE,"E0.rect.top");Q0=makeQuery(id+"F13.boolean.opBoolean","SPLIT",FACE,{"disambiguationData":[TD([makeQuery(id+"F1.opExtrude","SWEPT_FACE",FACE,{"disambiguationData":[OSD([subQ6])]})])],"derivedFrom":makeQuery(id+"F1.opExtrude","CAP_FACE",FACE,{"disambiguationData":[OSD([subQ7,subQ8,subQ6,sQuery(id+"F0.wireOp",EDGE,"E0.rect.right")])],"isStart":false})});}
            var sketch = newSketch(context, id + "F28", { "sketchPlane" : qUnion([Q0])});
            skLineSegment(sketch, "E108", {"start": v(1295.4, 660.4) * mm, "end": v(838.2, 1117.6) * mm});
            skLineSegment(sketch, "E109", {"start": v(838.2, 1117.6) * mm, "end": v(838.2, 660.4) * mm});
            skLineSegment(sketch, "E110", {"start": v(838.2, 660.4) * mm, "end": v(1295.4, 660.4) * mm, "construction": true});
            skLineSegment(sketch, "E111", {"start": v(-1295.4, 660.4) * mm, "end": v(-838.2, 660.4) * mm, "construction": true});
            skLineSegment(sketch, "E112", {"start": v(-838.2, 660.4) * mm, "end": v(-838.2, 1117.6) * mm});
            skLineSegment(sketch, "E113", {"start": v(-838.2, 1117.6) * mm, "end": v(-1295.4, 660.4) * mm});
            skLineSegment(sketch, "E114", {"start": v(1295.4, 660.4) * mm, "end": v(1295.4, 406.4) * mm});
            skLineSegment(sketch, "E115", {"start": v(1295.4, 406.4) * mm, "end": v(838.2, 406.4) * mm});
            skLineSegment(sketch, "E116", {"start": v(838.2, 406.4) * mm, "end": v(838.2, 660.4) * mm});
            skLineSegment(sketch, "E117", {"start": v(-1295.4, 660.4) * mm, "end": v(-1295.4, 406.4) * mm});
            skLineSegment(sketch, "E118", {"start": v(-1295.4, 406.4) * mm, "end": v(-838.2, 406.4) * mm});
            skLineSegment(sketch, "E119", {"start": v(-838.2, 406.4) * mm, "end": v(-838.2, 660.4) * mm});
            skSolve(sketch);
        }
        {
            var Q0;
            Q0 = qSketchRegion(id + "F28", true);
            extrude(context, id + "F29", {"entities" : qUnion([Q0]), "operationType" : NewBodyOperationType.ADD, "depth" : 9.52 * mm});
        }
        {
            var Q0;
            Q0=makeQuery(id+"F21.boolean.opBoolean","MERGE",FACE,{"derivedFrom":[makeQuery(id+"F20.opSweep","SWEPT_FACE",FACE,{"disambiguationData":[OSD([sQuery(id+"F14.wireOp",EDGE,"E66"),sQuery(id+"F17.wireOp",EDGE,"E76")])]}),makeQuery(id+"F21.opSweep","SWEPT_FACE",FACE,{"disambiguationData":[OSD([sQuery(id+"F14.wireOp",EDGE,"E63"),sQuery(id+"F17.wireOp",EDGE,"E91.MirrorCS")])]})]});
            var sketch = newSketch(context, id + "F30", { "sketchPlane" : qUnion([Q0])});
            skLineSegment(sketch, "E120", {"start": v(1295.4, -6105.53) * mm, "end": v(-1295.4, -6105.53) * mm});
            skLineSegment(sketch, "E121", {"start": v(-1295.4, -6105.53) * mm, "end": v(-1295.4, -8086.73) * mm});
            skLineSegment(sketch, "E122", {"start": v(-1295.4, -8086.73) * mm, "end": v(-838.2, -8543.93) * mm});
            skLineSegment(sketch, "E123", {"start": v(-838.2, -8543.93) * mm, "end": v(838.2, -8543.93) * mm});
            skLineSegment(sketch, "E124", {"start": v(838.2, -8543.93) * mm, "end": v(1295.4, -8086.73) * mm});
            skLineSegment(sketch, "E125", {"start": v(1295.4, -8086.73) * mm, "end": v(1295.4, -6105.53) * mm});
            skSolve(sketch);
        }
        {
            var Q0;
            Q0 = qSketchRegion(id + "F30", true);
            extrude(context, id + "F31", {"entities" : qUnion([Q0]), "depth" : 101.6 * mm});
        }
        {
            var Q0;
            {var subQ0=sQuery(id+"F2.wireOp",EDGE,"E4");var subQ1=sQuery(id+"F2.wireOp",EDGE,"E3");var subQ2=sQuery(id+"F2.wireOp",EDGE,"E2");var subQ3=sQuery(id+"F2.wireOp",EDGE,"E1");var subQ4=makeQuery(id+"F3.opExtrude","CAP_FACE",FACE,{"disambiguationData":[OSD([subQ3,subQ2,subQ1,subQ0])],"isStart":false});var subQ5=sQuery(id+"F0.wireOp",EDGE,"E0.rect.right");var subQ6=makeQuery(id+"F1.opExtrude","SWEPT_FACE",FACE,{"disambiguationData":[OSD([subQ5])]});var subQ7=makeQuery(id+"F3.opExtrude","CAP_FACE",FACE,{"disambiguationData":[OSD([subQ3,subQ2,subQ1,subQ0])],"isStart":true});var subQ8=sQuery(id+"F0.wireOp",EDGE,"E0.rect.left");var subQ9=makeQuery(id+"F1.opExtrude","SWEPT_FACE",FACE,{"disambiguationData":[OSD([subQ8])]});var subQ10=sQuery(id+"F4.wireOp",EDGE,"E6");var subQ11=makeQuery(id+"F5.opExtrude","SWEPT_FACE",FACE,{"disambiguationData":[OSD([subQ10])]});var subQ12=makeQuery(id+"F5.opExtrude","CAP_FACE",FACE,{"disambiguationData":[OSD([subQ10])],"isStart":true});var subQ13=makeQuery(id+"F5.opExtrude","CAP_FACE",FACE,{"disambiguationData":[OSD([subQ10])],"isStart":false});var subQ14=sQuery(id+"F4.wireOp",EDGE,"E7");var subQ15=makeQuery(id+"F5.opExtrude","SWEPT_FACE",FACE,{"disambiguationData":[OSD([subQ14])]});var subQ16=makeQuery(id+"F5.opExtrude","CAP_FACE",FACE,{"disambiguationData":[OSD([subQ14])],"isStart":true});var subQ17=makeQuery(id+"F5.opExtrude","CAP_FACE",FACE,{"disambiguationData":[OSD([subQ14])],"isStart":false});var subQ18=sQuery(id+"F0.wireOp",EDGE,"E0.rect.top");var subQ19=makeQuery(id+"F1.opExtrude","SWEPT_FACE",FACE,{"disambiguationData":[OSD([subQ18])]});var subQ20=sQuery(id+"F0.wireOp",EDGE,"E0.rect.bottom");Q0=makeQuery(id+"F29.boolean.opBoolean","MERGE",FACE,{"derivedFrom":[makeQuery(id+"F13.boolean.opBoolean","MERGE",FACE,{"derivedFrom":[makeQuery(id+"F7.boolean.opBoolean","MERGE",FACE,{"derivedFrom":[makeQuery(id+"F5.boolean.opBoolean","SPLIT",FACE,{"disambiguationData":[TD([makeQuery(id+"F1.opExtrude","CAP_FACE",FACE,{"disambiguationData":[OSD([subQ20,subQ18,subQ8,subQ5])],"isStart":true}),subQ9,subQ6,subQ7,subQ4,subQ11,subQ12,subQ13,subQ16,subQ17])],"derivedFrom":subQ19}),makeQuery(id+"F5.boolean.opBoolean","SPLIT",FACE,{"disambiguationData":[TD([makeQuery(id+"F1.opExtrude","CAP_FACE",FACE,{"disambiguationData":[OSD([subQ20,subQ18,subQ8,subQ5])],"isStart":false}),subQ9,subQ6,subQ7,subQ4,subQ12,subQ13,subQ15,subQ16,subQ17])],"derivedFrom":subQ19}),makeQuery(id+"F5.boolean.opBoolean","SPLIT",FACE,{"disambiguationData":[TD([subQ9,subQ6,subQ7,subQ4,subQ11,subQ12,subQ13,subQ15,subQ16,subQ17])],"derivedFrom":subQ19})],"fromTools":[makeQuery(id+"F7.opExtrude","SWEPT_FACE",FACE,{"disambiguationData":[OSD([sQuery(id+"F6.wireOp",EDGE,"E11.bottom")])]})]}),makeQuery(id+"F13.opExtrude","CAP_FACE",FACE,{"disambiguationData":[OSD([sQuery(id+"F12.wireOp",EDGE,"E36"),sQuery(id+"F12.wireOp",EDGE,"E37"),sQuery(id+"F12.wireOp",EDGE,"E38"),sQuery(id+"F12.wireOp",EDGE,"E39"),sQuery(id+"F12.wireOp",EDGE,"E40"),sQuery(id+"F12.wireOp",EDGE,"E41"),sQuery(id+"F12.wireOp",EDGE,"E42"),sQuery(id+"F12.wireOp",EDGE,"E43"),sQuery(id+"F12.wireOp",EDGE,"E44"),sQuery(id+"F12.wireOp",EDGE,"E45"),sQuery(id+"F12.wireOp",EDGE,"E46"),sQuery(id+"F12.wireOp",EDGE,"E47")])],"isStart":true}),makeQuery(id+"F13.opExtrude","CAP_FACE",FACE,{"disambiguationData":[OSD([sQuery(id+"F12.wireOp",EDGE,"E51.MirrorCS"),sQuery(id+"F12.wireOp",EDGE,"E52.MirrorCS"),sQuery(id+"F12.wireOp",EDGE,"E53.MirrorCS"),sQuery(id+"F12.wireOp",EDGE,"E54.MirrorCS"),sQuery(id+"F12.wireOp",EDGE,"E55.MirrorCS"),sQuery(id+"F12.wireOp",EDGE,"E56.MirrorCS"),sQuery(id+"F12.wireOp",EDGE,"E57.MirrorCS"),sQuery(id+"F12.wireOp",EDGE,"E58.MirrorCS"),sQuery(id+"F12.wireOp",EDGE,"E59.MirrorCS"),sQuery(id+"F12.wireOp",EDGE,"E60.MirrorCS"),sQuery(id+"F12.wireOp",EDGE,"E61.MirrorCS"),sQuery(id+"F12.wireOp",EDGE,"E62.MirrorCS")])],"isStart":true})]}),makeQuery(id+"F29.opExtrude","SWEPT_FACE",FACE,{"disambiguationData":[OSD([sQuery(id+"F28.wireOp",EDGE,"E115")])]}),makeQuery(id+"F29.opExtrude","SWEPT_FACE",FACE,{"disambiguationData":[OSD([sQuery(id+"F28.wireOp",EDGE,"E118")])]})]});}
            var sketch = newSketch(context, id + "F32", { "sketchPlane" : qUnion([Q0])});
            skCircle(sketch, "E126", {"center": v(0, 8739.02) * mm, "radius": 63.5 * mm});
            skSolve(sketch);
        }
        {
            var Q0;
            Q0=makeQuery(id+"F32.imprint","IMPRINT",FACE,{"disambiguationData":[TD([[makeQuery(id+"F32.imprint","IMPRINT",EDGE,{"derivedFrom":sQuery(id+"F32.wireOp",EDGE,"E126")}),1.0]])]});
            extrude(context, id + "F33", {"entities" : qUnion([Q0]), "operationType" : NewBodyOperationType.ADD, "oppositeDirection" : true, "depth" : 1473.2 * mm, "hasSecondDirection" : true, "secondDirectionOppositeDirection" : true, "secondDirectionDepth" : 914.4 * mm});
        }
        {
            var Q0;
            {var subQ0=sQuery(id+"F2.wireOp",EDGE,"E1");var subQ6=sQuery(id+"F0.wireOp",EDGE,"E0.rect.bottom");var subQ8=sQuery(id+"F2.wireOp",EDGE,"E3");var subQ12=makeQuery(id+"F1.opExtrude","SWEPT_FACE",FACE,{"disambiguationData":[OSD([subQ6])]});Q0=makeQuery(id+"F7.boolean.opBoolean","MERGE",FACE,{"derivedFrom":[makeQuery(id+"F3.boolean.opBoolean","SPLIT",FACE,{"disambiguationData":[TD([makeQuery(id+"F3.opExtrude","SWEPT_FACE",FACE,{"disambiguationData":[OSD([subQ8])]})])],"derivedFrom":subQ12}),makeQuery(id+"F3.boolean.opBoolean","SPLIT",FACE,{"disambiguationData":[TD([makeQuery(id+"F3.opExtrude","SWEPT_FACE",FACE,{"disambiguationData":[OSD([subQ0])]})])],"derivedFrom":subQ12})],"fromTools":[makeQuery(id+"F7.opExtrude","SWEPT_FACE",FACE,{"disambiguationData":[OSD([sQuery(id+"F6.wireOp",EDGE,"E10.top")])]})]});}
            var sketch = newSketch(context, id + "F34", { "sketchPlane" : qUnion([Q0])});
            skLineSegment(sketch, "E127", {"start": v(-1143, -5943.6) * mm, "end": v(1143, -5943.6) * mm});
            skLineSegment(sketch, "E128", {"start": v(1143, -5943.6) * mm, "end": v(1143, -3467.1) * mm});
            skLineSegment(sketch, "E129", {"start": v(1143, -3467.1) * mm, "end": v(882.65, -3467.1) * mm});
            skLineSegment(sketch, "E130", {"start": v(882.65, -3467.1) * mm, "end": v(882.65, -800.1) * mm});
            skLineSegment(sketch, "E131", {"start": v(882.65, -800.1) * mm, "end": v(1143, -800.1) * mm});
            skLineSegment(sketch, "E132", {"start": v(1143, -800.1) * mm, "end": v(1143, -152.4) * mm});
            skLineSegment(sketch, "E133", {"start": v(1143, -152.4) * mm, "end": v(-1143, -152.4) * mm});
            skLineSegment(sketch, "E134", {"start": v(-1143, -152.4) * mm, "end": v(-1143, -800.1) * mm});
            skLineSegment(sketch, "E135", {"start": v(-1143, -800.1) * mm, "end": v(-882.65, -800.1) * mm});
            skLineSegment(sketch, "E136", {"start": v(-882.65, -800.1) * mm, "end": v(-882.65, -3467.1) * mm});
            skLineSegment(sketch, "E137", {"start": v(-882.65, -3467.1) * mm, "end": v(-1143, -3467.1) * mm});
            skLineSegment(sketch, "E138", {"start": v(-1143, -3467.1) * mm, "end": v(-1143, -5943.6) * mm});
            skLineSegment(sketch, "E139", {"start": v(-1143, -4705.35) * mm, "end": v(-1295.4, -4705.35) * mm, "construction": true});
            skLineSegment(sketch, "E140", {"start": v(0, -5943.6) * mm, "end": v(0, -6096) * mm, "construction": true});
            skLineSegment(sketch, "E141", {"start": v(1143, -4705.35) * mm, "end": v(1295.4, -4705.35) * mm, "construction": true});
            skLineSegment(sketch, "E142", {"start": v(882.65, -2133.6) * mm, "end": v(1035.05, -2133.6) * mm, "construction": true});
            skLineSegment(sketch, "E143", {"start": v(-882.65, -2133.6) * mm, "end": v(-1035.05, -2133.6) * mm, "construction": true});
            skLineSegment(sketch, "E144", {"start": v(0, -152.4) * mm, "end": v(0, 0) * mm, "construction": true});
            skLineSegment(sketch, "E145", {"start": v(1295.4, -476.25) * mm, "end": v(1143, -476.25) * mm, "construction": true});
            skLineSegment(sketch, "E146", {"start": v(-1143, -476.25) * mm, "end": v(-1295.4, -476.25) * mm, "construction": true});
            skLineSegment(sketch, "E147", {"start": v(-1143, -3467.1) * mm, "end": v(-1143, -3314.7) * mm, "construction": true});
            skLineSegment(sketch, "E148", {"start": v(1143, -3467.1) * mm, "end": v(1143, -3314.7) * mm, "construction": true});
            skLineSegment(sketch, "E149", {"start": v(1143, -800.1) * mm, "end": v(1143, -952.5) * mm, "construction": true});
            skPoint(sketch, "E149.endSnap0", {"position": v(1165.23, -952.5) * mm});
            skLineSegment(sketch, "E150", {"start": v(-1143, -800.1) * mm, "end": v(-1143, -952.5) * mm, "construction": true});
            skSolve(sketch);
        }
        {
            var Q0;
            Q0=makeQuery(id+"F34.imprint","IMPRINT",FACE,{"disambiguationData":[TD([[makeQuery(id+"F34.imprint","IMPRINT",EDGE,{"derivedFrom":sQuery(id+"F34.wireOp",EDGE,"E127")}),1.0]])]});
            extrude(context, id + "F35", {"entities" : qUnion([Q0]), "operationType" : NewBodyOperationType.REMOVE, "oppositeDirection" : true, "depth" : 38.1 * mm});
        }
        {
            var Q0;
            Q0=makeQuery(id+"F31.opExtrude","CAP_FACE",FACE,{"disambiguationData":[OSD([sQuery(id+"F30.wireOp",EDGE,"E120"),sQuery(id+"F30.wireOp",EDGE,"E121"),sQuery(id+"F30.wireOp",EDGE,"E122"),sQuery(id+"F30.wireOp",EDGE,"E123"),sQuery(id+"F30.wireOp",EDGE,"E124"),sQuery(id+"F30.wireOp",EDGE,"E125")])],"isStart":false});
            var sketch = newSketch(context, id + "F36", { "sketchPlane" : qUnion([Q0])});
            skLineSegment(sketch, "E151.0", {"start": v(1289.05, -8084.1) * mm, "end": v(1289.05, -3327.4) * mm});
            skLineSegment(sketch, "E151.1", {"start": v(-1289.05, -3327.4) * mm, "end": v(-1289.05, -8084.1) * mm});
            skLineSegment(sketch, "E151.2", {"start": v(-1289.05, -8084.1) * mm, "end": v(-835.57, -8537.57) * mm});
            skLineSegment(sketch, "E151.3", {"start": v(-835.57, -8537.57) * mm, "end": v(835.57, -8537.57) * mm});
            skLineSegment(sketch, "E151.4", {"start": v(835.57, -8537.57) * mm, "end": v(1289.05, -8084.1) * mm});
            skLineSegment(sketch, "E152", {"start": v(1289.05, -939.8) * mm, "end": v(1289.05, -12.7) * mm});
            skLineSegment(sketch, "E153", {"start": v(-1244.6, -12.7) * mm, "end": v(-1244.6, -939.8) * mm});
            skLineSegment(sketch, "E154", {"start": v(-1244.6, -12.7) * mm, "end": v(-1289.05, -12.7) * mm});
            skLineSegment(sketch, "E155", {"start": v(-1289.05, -12.7) * mm, "end": v(-1289.05, -939.8) * mm});
            skLineSegment(sketch, "E156", {"start": v(-1289.05, -939.8) * mm, "end": v(-1244.6, -939.8) * mm});
            skLineSegment(sketch, "E157", {"start": v(1289.05, -939.8) * mm, "end": v(1244.6, -939.8) * mm});
            skLineSegment(sketch, "E158", {"start": v(1244.6, -939.8) * mm, "end": v(1244.6, -12.7) * mm});
            skLineSegment(sketch, "E159", {"start": v(1244.6, -12.7) * mm, "end": v(1289.05, -12.7) * mm});
            skLineSegment(sketch, "E160", {"start": v(-1289.05, -3327.4) * mm, "end": v(-1244.6, -3327.4) * mm});
            skLineSegment(sketch, "E161", {"start": v(-1244.6, -3327.4) * mm, "end": v(-1244.6, -8065.68) * mm});
            skLineSegment(sketch, "E162", {"start": v(-1244.6, -8065.68) * mm, "end": v(-817.16, -8493.13) * mm});
            skLineSegment(sketch, "E163", {"start": v(-817.16, -8493.13) * mm, "end": v(817.16, -8493.13) * mm});
            skLineSegment(sketch, "E164", {"start": v(817.16, -8493.13) * mm, "end": v(1244.6, -8065.68) * mm});
            skLineSegment(sketch, "E165", {"start": v(1244.6, -8065.68) * mm, "end": v(1244.6, -3327.4) * mm});
            skLineSegment(sketch, "E166", {"start": v(1244.6, -3327.4) * mm, "end": v(1289.05, -3327.4) * mm});
            skLineSegment(sketch, "E167", {"start": v(-1244.6, -8065.68) * mm, "end": v(-1289.05, -8065.68) * mm, "construction": true});
            skLineSegment(sketch, "E168", {"start": v(-1030.88, -8279.4) * mm, "end": v(-1062.3, -8310.83) * mm, "construction": true});
            skLineSegment(sketch, "E169", {"start": v(0, -8493.13) * mm, "end": v(0, -8537.57) * mm, "construction": true});
            skLineSegment(sketch, "E170", {"start": v(1030.88, -8279.4) * mm, "end": v(1062.3, -8310.83) * mm, "construction": true});
            skLineSegment(sketch, "E171", {"start": v(-1244.6, -3562.35) * mm, "end": v(-1289.05, -3562.35) * mm});
            skLineSegment(sketch, "E172", {"start": v(-1244.6, -4178.3) * mm, "end": v(-1289.05, -4178.3) * mm});
            skLineSegment(sketch, "E173", {"start": v(-1244.6, -4794.25) * mm, "end": v(-1289.05, -4794.25) * mm});
            skLineSegment(sketch, "E174", {"start": v(-1244.6, -5410.2) * mm, "end": v(-1289.05, -5410.2) * mm});
            skLineSegment(sketch, "E175", {"start": v(-1244.6, -6019.8) * mm, "end": v(-1289.05, -6019.8) * mm});
            skLineSegment(sketch, "E176", {"start": v(-1244.6, -5403.85) * mm, "end": v(-1289.05, -5403.85) * mm});
            skLineSegment(sketch, "E177", {"start": v(-1244.6, -4787.9) * mm, "end": v(-1289.05, -4787.9) * mm});
            skLineSegment(sketch, "E178", {"start": v(-1244.6, -4171.95) * mm, "end": v(-1289.05, -4171.95) * mm});
            skLineSegment(sketch, "E179", {"start": v(-1244.6, -3556) * mm, "end": v(-1289.05, -3556) * mm});
            skLineSegment(sketch, "E180", {"start": v(-1289.05, -6181.73) * mm, "end": v(-1244.6, -6181.73) * mm});
            skLineSegment(sketch, "E181", {"start": v(-1289.05, -6791.33) * mm, "end": v(-1244.6, -6791.33) * mm});
            skLineSegment(sketch, "E182", {"start": v(-1289.05, -6797.68) * mm, "end": v(-1244.6, -6797.68) * mm});
            skLineSegment(sketch, "E183", {"start": v(-1289.05, -7407.28) * mm, "end": v(-1244.6, -7407.28) * mm});
            skLineSegment(sketch, "E184", {"start": v(-1289.05, -7413.63) * mm, "end": v(-1244.6, -7413.63) * mm});
            skLineSegment(sketch, "E185", {"start": v(-1244.6, -8023.23) * mm, "end": v(-1289.05, -8023.23) * mm});
            skLineSegment(sketch, "E186", {"start": v(-1228.44, -8081.84) * mm, "end": v(-1259.88, -8113.27) * mm});
            skLineSegment(sketch, "E187", {"start": v(-833.31, -8476.97) * mm, "end": v(-864.74, -8508.4) * mm});
            skLineSegment(sketch, "E188", {"start": v(-1259.88, -8113.27) * mm, "end": v(-1030.88, -8279.4) * mm, "construction": true});
            skLineSegment(sketch, "E189", {"start": v(-864.74, -8508.4) * mm, "end": v(-1030.88, -8279.4) * mm, "construction": true});
            skLineSegment(sketch, "E190", {"start": v(-768.35, -8493.13) * mm, "end": v(-768.35, -8537.57) * mm});
            skLineSegment(sketch, "E191", {"start": v(-311.15, -8537.57) * mm, "end": v(-311.15, -8493.13) * mm});
            skLineSegment(sketch, "E192", {"start": v(-304.8, -8537.57) * mm, "end": v(-304.8, -8493.13) * mm});
            skLineSegment(sketch, "E193", {"start": v(304.8, -8493.13) * mm, "end": v(304.8, -8537.57) * mm});
            skLineSegment(sketch, "E194", {"start": v(311.15, -8493.13) * mm, "end": v(311.15, -8537.57) * mm});
            skLineSegment(sketch, "E195", {"start": v(768.35, -8493.13) * mm, "end": v(768.35, -8537.57) * mm});
            skLineSegment(sketch, "E196", {"start": v(768.35, -8493.12) * mm, "end": v(835.57, -8537.57) * mm, "construction": true});
            skLineSegment(sketch, "E197", {"start": v(311.15, -8537.57) * mm, "end": v(768.35, -8493.12) * mm, "construction": true});
            skLineSegment(sketch, "E198", {"start": v(-768.35, -8493.13) * mm, "end": v(-311.15, -8537.57) * mm, "construction": true});
            skLineSegment(sketch, "E199", {"start": v(-768.35, -8493.13) * mm, "end": v(-835.57, -8537.57) * mm, "construction": true});
            skLineSegment(sketch, "E200", {"start": v(833.31, -8476.97) * mm, "end": v(864.74, -8508.4) * mm});
            skLineSegment(sketch, "E201", {"start": v(1228.44, -8081.84) * mm, "end": v(1259.88, -8113.27) * mm});
            skLineSegment(sketch, "E202", {"start": v(864.74, -8508.4) * mm, "end": v(1030.88, -8279.4) * mm, "construction": true});
            skLineSegment(sketch, "E203", {"start": v(1259.88, -8113.27) * mm, "end": v(1030.88, -8279.4) * mm, "construction": true});
            skLineSegment(sketch, "E204", {"start": v(1244.6, -8023.23) * mm, "end": v(1289.05, -8023.23) * mm});
            skLineSegment(sketch, "E205", {"start": v(1244.6, -7413.63) * mm, "end": v(1289.05, -7413.63) * mm});
            skLineSegment(sketch, "E206", {"start": v(1244.6, -7407.28) * mm, "end": v(1289.05, -7407.28) * mm});
            skLineSegment(sketch, "E207", {"start": v(1244.6, -6797.68) * mm, "end": v(1289.05, -6797.68) * mm});
            skLineSegment(sketch, "E208", {"start": v(1244.6, -6791.33) * mm, "end": v(1289.05, -6791.33) * mm});
            skLineSegment(sketch, "E209", {"start": v(1244.6, -6181.73) * mm, "end": v(1289.05, -6181.73) * mm});
            skLineSegment(sketch, "E210", {"start": v(1244.6, -6019.8) * mm, "end": v(1289.05, -6019.8) * mm});
            skLineSegment(sketch, "E211", {"start": v(1244.6, -5410.2) * mm, "end": v(1289.05, -5410.2) * mm});
            skLineSegment(sketch, "E212", {"start": v(1244.6, -5403.85) * mm, "end": v(1289.05, -5403.85) * mm});
            skLineSegment(sketch, "E213", {"start": v(1244.6, -4794.25) * mm, "end": v(1289.05, -4794.25) * mm});
            skLineSegment(sketch, "E214", {"start": v(1244.6, -4787.9) * mm, "end": v(1289.05, -4787.9) * mm});
            skLineSegment(sketch, "E215", {"start": v(1244.6, -4178.3) * mm, "end": v(1289.05, -4178.3) * mm});
            skLineSegment(sketch, "E216", {"start": v(1244.6, -4171.95) * mm, "end": v(1289.05, -4171.95) * mm});
            skLineSegment(sketch, "E217", {"start": v(1244.6, -3562.35) * mm, "end": v(1289.05, -3562.35) * mm});
            skLineSegment(sketch, "E218", {"start": v(1244.6, -3556) * mm, "end": v(1289.05, -3556) * mm});
            skSolve(sketch);
        }
        {
            var Q0;
            {var subQ0=sQuery(id+"F36.wireOp",EDGE,"E190");Q0=makeQuery(id+"F36.imprint","IMPRINT",FACE,{"disambiguationData":[TD([[makeQuery(id+"F36.imprint","IMPRINT",EDGE,{"derivedFrom":subQ0}),1.0]])]});}
            var Q1;
            {var subQ0=sQuery(id+"F36.wireOp",EDGE,"E194");Q1=makeQuery(id+"F36.imprint","IMPRINT",FACE,{"disambiguationData":[TD([[makeQuery(id+"F36.imprint","IMPRINT",EDGE,{"derivedFrom":subQ0}),1.0]])]});}
            var Q2;
            {var subQ0=sQuery(id+"F36.wireOp",EDGE,"E200");Q2=makeQuery(id+"F36.imprint","IMPRINT",FACE,{"disambiguationData":[TD([[makeQuery(id+"F36.imprint","IMPRINT",EDGE,{"derivedFrom":subQ0}),1.0]])]});}
            var Q3;
            {var subQ0=sQuery(id+"F36.wireOp",EDGE,"E204");Q3=makeQuery(id+"F36.imprint","IMPRINT",FACE,{"disambiguationData":[TD([[makeQuery(id+"F36.imprint","IMPRINT",EDGE,{"derivedFrom":subQ0}),1.0]])]});}
            var Q4;
            {var subQ0=sQuery(id+"F36.wireOp",EDGE,"E206");Q4=makeQuery(id+"F36.imprint","IMPRINT",FACE,{"disambiguationData":[TD([[makeQuery(id+"F36.imprint","IMPRINT",EDGE,{"derivedFrom":subQ0}),1.0]])]});}
            var Q5;
            {var subQ0=sQuery(id+"F36.wireOp",EDGE,"E208");Q5=makeQuery(id+"F36.imprint","IMPRINT",FACE,{"disambiguationData":[TD([[makeQuery(id+"F36.imprint","IMPRINT",EDGE,{"derivedFrom":subQ0}),1.0]])]});}
            var Q6;
            {var subQ0=sQuery(id+"F36.wireOp",EDGE,"E210");Q6=makeQuery(id+"F36.imprint","IMPRINT",FACE,{"disambiguationData":[TD([[makeQuery(id+"F36.imprint","IMPRINT",EDGE,{"derivedFrom":subQ0}),1.0]])]});}
            var Q7;
            {var subQ0=sQuery(id+"F36.wireOp",EDGE,"E212");Q7=makeQuery(id+"F36.imprint","IMPRINT",FACE,{"disambiguationData":[TD([[makeQuery(id+"F36.imprint","IMPRINT",EDGE,{"derivedFrom":subQ0}),1.0]])]});}
            var Q8;
            {var subQ0=sQuery(id+"F36.wireOp",EDGE,"E214");Q8=makeQuery(id+"F36.imprint","IMPRINT",FACE,{"disambiguationData":[TD([[makeQuery(id+"F36.imprint","IMPRINT",EDGE,{"derivedFrom":subQ0}),1.0]])]});}
            var Q9;
            {var subQ0=sQuery(id+"F36.wireOp",EDGE,"E216");Q9=makeQuery(id+"F36.imprint","IMPRINT",FACE,{"disambiguationData":[TD([[makeQuery(id+"F36.imprint","IMPRINT",EDGE,{"derivedFrom":subQ0}),1.0]])]});}
            var Q10;
            {var subQ0=sQuery(id+"F36.wireOp",EDGE,"E166");Q10=makeQuery(id+"F36.imprint","IMPRINT",FACE,{"disambiguationData":[TD([[makeQuery(id+"F36.imprint","IMPRINT",EDGE,{"derivedFrom":subQ0}),-1.0]])]});}
            var Q11;
            Q11=makeQuery(id+"F36.imprint","IMPRINT",FACE,{"disambiguationData":[TD([[makeQuery(id+"F36.imprint","IMPRINT",EDGE,{"derivedFrom":sQuery(id+"F36.wireOp",EDGE,"E152")}),1.0]])]});
            var Q12;
            Q12=makeQuery(id+"F36.imprint","IMPRINT",FACE,{"disambiguationData":[TD([[makeQuery(id+"F36.imprint","IMPRINT",EDGE,{"derivedFrom":sQuery(id+"F36.wireOp",EDGE,"E153")}),-1.0]])]});
            var Q13;
            {var subQ0=sQuery(id+"F36.wireOp",EDGE,"E160");Q13=makeQuery(id+"F36.imprint","IMPRINT",FACE,{"disambiguationData":[TD([[makeQuery(id+"F36.imprint","IMPRINT",EDGE,{"derivedFrom":subQ0}),-1.0]])]});}
            var Q14;
            {var subQ0=sQuery(id+"F36.wireOp",EDGE,"E171");Q14=makeQuery(id+"F36.imprint","IMPRINT",FACE,{"disambiguationData":[TD([[makeQuery(id+"F36.imprint","IMPRINT",EDGE,{"derivedFrom":subQ0}),1.0]])]});}
            var Q15;
            {var subQ0=sQuery(id+"F36.wireOp",EDGE,"E172");Q15=makeQuery(id+"F36.imprint","IMPRINT",FACE,{"disambiguationData":[TD([[makeQuery(id+"F36.imprint","IMPRINT",EDGE,{"derivedFrom":subQ0}),1.0]])]});}
            var Q16;
            {var subQ0=sQuery(id+"F36.wireOp",EDGE,"E173");Q16=makeQuery(id+"F36.imprint","IMPRINT",FACE,{"disambiguationData":[TD([[makeQuery(id+"F36.imprint","IMPRINT",EDGE,{"derivedFrom":subQ0}),1.0]])]});}
            var Q17;
            {var subQ0=sQuery(id+"F36.wireOp",EDGE,"E174");Q17=makeQuery(id+"F36.imprint","IMPRINT",FACE,{"disambiguationData":[TD([[makeQuery(id+"F36.imprint","IMPRINT",EDGE,{"derivedFrom":subQ0}),1.0]])]});}
            var Q18;
            {var subQ0=sQuery(id+"F36.wireOp",EDGE,"E180");Q18=makeQuery(id+"F36.imprint","IMPRINT",FACE,{"disambiguationData":[TD([[makeQuery(id+"F36.imprint","IMPRINT",EDGE,{"derivedFrom":subQ0}),-1.0]])]});}
            var Q19;
            {var subQ0=sQuery(id+"F36.wireOp",EDGE,"E182");Q19=makeQuery(id+"F36.imprint","IMPRINT",FACE,{"disambiguationData":[TD([[makeQuery(id+"F36.imprint","IMPRINT",EDGE,{"derivedFrom":subQ0}),-1.0]])]});}
            var Q20;
            {var subQ0=sQuery(id+"F36.wireOp",EDGE,"E184");Q20=makeQuery(id+"F36.imprint","IMPRINT",FACE,{"disambiguationData":[TD([[makeQuery(id+"F36.imprint","IMPRINT",EDGE,{"derivedFrom":subQ0}),-1.0]])]});}
            var Q21;
            {var subQ0=sQuery(id+"F36.wireOp",EDGE,"E186");Q21=makeQuery(id+"F36.imprint","IMPRINT",FACE,{"disambiguationData":[TD([[makeQuery(id+"F36.imprint","IMPRINT",EDGE,{"derivedFrom":subQ0}),1.0]])]});}
            extrude(context, id + "F37", {"entities" : qUnion([Q0, Q1, Q2, Q3, Q4, Q5, Q6, Q7, Q8, Q9, Q10, Q11, Q12, Q13, Q14, Q15, Q16, Q17, Q18, Q19, Q20, Q21]), "operationType" : NewBodyOperationType.REMOVE, "endBound" : BoundingType.THROUGH_ALL, "oppositeDirection" : true, "depth" : 25.4 * mm});
        }
        {
            var Q0;
            {var subQ0=sQuery(id+"F36.wireOp",EDGE,"E192");Q0=makeQuery(id+"F36.imprint","IMPRINT",FACE,{"disambiguationData":[TD([[makeQuery(id+"F36.imprint","IMPRINT",EDGE,{"derivedFrom":subQ0}),-1.0]])]});}
            extrude(context, id + "F38", {"entities" : qUnion([Q0]), "operationType" : NewBodyOperationType.REMOVE, "endBound" : BoundingType.UP_TO_NEXT, "oppositeDirection" : true, "depth" : 25.4 * mm});
        }
        {
            var Q0;
            Q0=makeQuery(id+"F29.boolean.opBoolean","MERGE",FACE,{"derivedFrom":[makeQuery(id+"F13.opExtrude","SWEPT_FACE",FACE,{"disambiguationData":[OSD([sQuery(id+"F12.wireOp",EDGE,"E37")])]}),makeQuery(id+"F29.opExtrude","CAP_FACE",FACE,{"disambiguationData":[OSD([sQuery(id+"F28.wireOp",EDGE,"E108"),sQuery(id+"F28.wireOp",EDGE,"E109"),sQuery(id+"F28.wireOp",EDGE,"E114"),sQuery(id+"F28.wireOp",EDGE,"E115"),sQuery(id+"F28.wireOp",EDGE,"E116")])],"isStart":false})]});
            var sketch = newSketch(context, id + "F39", { "sketchPlane" : qUnion([Q0])});
            skLineSegment(sketch, "E219", {"start": v(1295.4, 533.4) * mm, "end": v(838.2, 406.4) * mm});
            skLineSegment(sketch, "E220", {"start": v(838.2, 406.4) * mm, "end": v(1295.4, 406.4) * mm});
            skLineSegment(sketch, "E221", {"start": v(1295.4, 406.4) * mm, "end": v(1295.4, 533.4) * mm});
            skLineSegment(sketch, "E222", {"start": v(-1295.4, 533.4) * mm, "end": v(-838.2, 406.4) * mm});
            skLineSegment(sketch, "E223", {"start": v(-838.2, 406.4) * mm, "end": v(-1295.4, 406.4) * mm});
            skLineSegment(sketch, "E224", {"start": v(-1295.4, 406.4) * mm, "end": v(-1295.4, 533.4) * mm});
            skSolve(sketch);
        }
        {
            var Q0;
            Q0 = qSketchRegion(id + "F39", true);
            var Q1;
            Q1=makeQuery(id+"F11.boolean.opBoolean","COPY",FACE,{"derivedFrom":makeQuery(id+"F11.opExtrude","SWEPT_FACE",FACE,{"disambiguationData":[OSD([sQuery(id+"F10.wireOp",EDGE,"E29")])]})});
            extrude(context, id + "F40", {"entities" : qUnion([Q0]), "operationType" : NewBodyOperationType.REMOVE, "endBound" : BoundingType.UP_TO_SURFACE, "oppositeDirection" : true, "endBoundEntityFace" : qUnion([Q1]), "depth" : 25.4 * mm});
        }
        {
            var Q0;
            Q0=makeQuery(id+"F1.opExtrude","CAP_FACE",FACE,{"disambiguationData":[OSD([sQuery(id+"F0.wireOp",EDGE,"E0.rect.bottom"),sQuery(id+"F0.wireOp",EDGE,"E0.rect.top"),sQuery(id+"F0.wireOp",EDGE,"E0.rect.left"),sQuery(id+"F0.wireOp",EDGE,"E0.rect.right")])],"isStart":true});
            var sketch = newSketch(context, id + "F41", { "sketchPlane" : qUnion([Q0])});
            skLineSegment(sketch, "E225", {"start": v(1295.4, 533.4) * mm, "end": v(838.2, 406.4) * mm});
            skLineSegment(sketch, "E226", {"start": v(838.2, 406.4) * mm, "end": v(1295.4, 406.4) * mm});
            skLineSegment(sketch, "E227", {"start": v(1295.4, 406.4) * mm, "end": v(1295.4, 533.4) * mm});
            skLineSegment(sketch, "E228", {"start": v(-838.2, 406.4) * mm, "end": v(-1295.4, 406.4) * mm});
            skLineSegment(sketch, "E229", {"start": v(-1295.4, 406.4) * mm, "end": v(-1295.4, 533.4) * mm});
            skLineSegment(sketch, "E230", {"start": v(-1295.4, 533.4) * mm, "end": v(-838.2, 406.4) * mm});
            skSolve(sketch);
        }
        {
            var Q0;
            Q0=makeQuery(id+"F41.imprint","IMPRINT",FACE,{"disambiguationData":[TD([[makeQuery(id+"F41.imprint","IMPRINT",EDGE,{"derivedFrom":sQuery(id+"F41.wireOp",EDGE,"E228")}),1.0]])]});
            var Q1;
            Q1=makeQuery(id+"F41.imprint","IMPRINT",FACE,{"disambiguationData":[TD([[makeQuery(id+"F41.imprint","IMPRINT",EDGE,{"derivedFrom":sQuery(id+"F41.wireOp",EDGE,"E225")}),1.0]])]});
            var Q2;
            Q2=makeQuery(id+"F9.boolean.opBoolean","COPY",FACE,{"derivedFrom":makeQuery(id+"F9.opExtrude","SWEPT_FACE",FACE,{"disambiguationData":[OSD([sQuery(id+"F8.wireOp",EDGE,"E19")])]})});
            extrude(context, id + "F42", {"entities" : qUnion([Q0, Q1]), "operationType" : NewBodyOperationType.REMOVE, "endBound" : BoundingType.UP_TO_SURFACE, "oppositeDirection" : true, "endBoundEntityFace" : qUnion([Q2]), "depth" : 25.4 * mm});
        }
    });
